# Revit family: xxxSink-Bubbler_Basin-Drop_In-ADA-Acorn-SDADA-3322_Series
name_source: partatom
category: Plumbing Fixtures
units: mm (PartAtom-declared; Revit-internal decimal feet)

## family parameters
Cut with Voids When Loaded = No
Host = Face
OmniClass Number = 23.45.05.14.14
OmniClass Title = Sinks/Lavatories
Part Type = Normal
Room Calculation Point = No
Round Connector Dimension = Use Diameter
Shared = Yes

## types (24) — shared parameters
ADA Compliant = Yes
Assembly Code = D2010440
CW Connection = No
CWFU = 3
Compliance Certifications = ASME A112.19.3/CSA B45.4, IAPMO® Certified for Conformance with Uniform Plumbing Code (UPC ), International Plumbing Code (IPC ), National Plumbing Code of Canada (NPC )
Default Elevation = 34"
Description = Acorn-Sinks® Stainless Steel ADA Drop-In Sink, 33" x 22"
Drain Size = 2"
Finish = Stainless Steel-18 Gauge-Type 304-Acorn-Satin
HW Connection = No
HWFU = 3
Installation Type = Drop-In Counter
Length = 22"
Manufacturer = Acorn
Product Documentation Link = https://www.acorneng.com
Product Page URL = https://www.acorneng.com
Sink Bowl Length = 16"
Sink Bowl Width = 28"
URL = https://www.acorneng.com
Vent Connection = No
WFU = 4
Waste Connection = No
Width = 33"
cUPC Compliant = Yes

## per-type parameters (varying)
| type | -0 Blank, No Deck Punching | -1 | -1 Single Hole Centered | -2 | -2 2 Holes on 4” Centers (4” Centerset) | -2R | -2R Single Hole Centered w/ 2nd Hole 4” to Right | -3 | -3 3 Holes on 4” Centers (8” Centerset) | -4 | -45 4-1/2” Deep Bowl | -4L 3 Holes on 4” Centers w/ 4th Hole 4” to Left | -4R 3 Holes on 4” Centers w/ 4th Hole 4” to Right | -5 | -5 5 Holes on 4” Centers | -55 5-1/2” Deep Bowl | -65 6-1/2” Deep Bowl | Sink Bowl Depth |
| SDADA-3322-65-0 | Yes | 1/2" | No | 16 1/2" | No | 1/2" | No | 1/2" | No | 1/2" | No | No | No | 1/2" | No | No | Yes | 6 1/2" |
| SDADA-3322-65-1 | No | 0" | Yes | 16 1/2" | No | 1/2" | No | 1/2" | No | 1/2" | No | No | No | 1/2" | No | No | Yes | 6 1/2" |
| SDADA-3322-65-2 | No | 0" | No | 18 1/2" | Yes | 0" | No | 1/2" | No | 1/2" | No | No | No | 1/2" | No | No | Yes | 6 1/2" |
| SDADA-3322-65-2R | No | 0" | No | 16 1/2" | No | 0" | Yes | 1/2" | No | 1/2" | No | No | No | 1/2" | No | No | Yes | 6 1/2" |
| SDADA-3322-65-3 | No | 0" | No | 16 1/2" | No | 0" | No | 0" | Yes | 1/2" | No | No | No | 1/2" | No | No | Yes | 6 1/2" |
| SDADA-3322-65-4L | No | 0" | No | 16 1/2" | No | 0" | No | 0" | No | 0" | No | Yes | No | 1/2" | No | No | Yes | 6 1/2" |
| SDADA-3322-65-4R | No | 0" | No | 12 1/2" | No | 0" | No | 0" | No | 0" | No | No | Yes | 1/2" | No | No | Yes | 6 1/2" |
| SDADA-3322-65-5 | No | 0" | No | 16 1/2" | No | 0" | No | 0" | No | 0" | No | No | No | 0" | Yes | No | Yes | 6 1/2" |
| SDADA-3322-55-5 | No | 0" | No | 16 1/2" | No | 0" | No | 0" | No | 0" | No | No | No | 0" | Yes | Yes | No | 5 1/2" |
| SDADA-3322-55-4L | No | 0" | No | 16 1/2" | No | 0" | No | 0" | No | 0" | No | Yes | No | 1/2" | No | Yes | No | 5 1/2" |
| SDADA-3322-55-4R | No | 0" | No | 12 1/2" | No | 0" | No | 0" | No | 0" | No | No | Yes | 1/2" | No | Yes | No | 5 1/2" |
| SDADA-3322-55-3 | No | 0" | No | 16 1/2" | No | 0" | No | 0" | Yes | 1/2" | No | No | No | 1/2" | No | Yes | No | 5 1/2" |
| SDADA-3322-55-2R | No | 0" | No | 16 1/2" | No | 0" | Yes | 1/2" | No | 1/2" | No | No | No | 1/2" | No | Yes | No | 5 1/2" |
| SDADA-3322-55-2 | No | 0" | No | 18 1/2" | Yes | 0" | No | 1/2" | No | 1/2" | No | No | No | 1/2" | No | Yes | No | 5 1/2" |
| SDADA-3322-55-1 | No | 0" | Yes | 16 1/2" | No | 1/2" | No | 1/2" | No | 1/2" | No | No | No | 1/2" | No | Yes | No | 5 1/2" |
| SDADA-3322-55-0 | Yes | 1/2" | No | 16 1/2" | No | 1/2" | No | 1/2" | No | 1/2" | No | No | No | 1/2" | No | Yes | No | 5 1/2" |
| SDADA-3322-45-0 | Yes | 1/2" | No | 16 1/2" | No | 1/2" | No | 1/2" | No | 1/2" | Yes | No | No | 1/2" | No | No | No | 4 1/2" |
| SDADA-3322-45-1 | No | 0" | Yes | 16 1/2" | No | 1/2" | No | 1/2" | No | 1/2" | Yes | No | No | 1/2" | No | No | No | 4 1/2" |
| SDADA-3322-45-2R | No | 0" | No | 16 1/2" | No | 0" | Yes | 1/2" | No | 1/2" | Yes | No | No | 1/2" | No | No | No | 4 1/2" |
| SDADA-3322-45-2 | No | 0" | No | 18 1/2" | Yes | 0" | No | 1/2" | No | 1/2" | Yes | No | No | 1/2" | No | No | No | 4 1/2" |
| SDADA-3322-45-3 | No | 0" | No | 16 1/2" | No | 0" | No | 0" | Yes | 1/2" | Yes | No | No | 1/2" | No | No | No | 4 1/2" |
| SDADA-3322-45-4L | No | 0" | No | 16 1/2" | No | 0" | No | 0" | No | 0" | Yes | Yes | No | 1/2" | No | No | No | 4 1/2" |
| SDADA-3322-45-4R | No | 0" | No | 12 1/2" | No | 0" | No | 0" | No | 0" | Yes | No | Yes | 1/2" | No | No | No | 4 1/2" |
| SDADA-3322-45-5 | No | 0" | No | 16 1/2" | No | 0" | No | 0" | No | 0" | Yes | No | No | 0" | Yes | No | No | 4 1/2" |

note: column(s) folded — value = type name in every type: Model

## geometry (parser evidence)
native form markers: Sweep x3
no freeform markers — native parametric forms only
